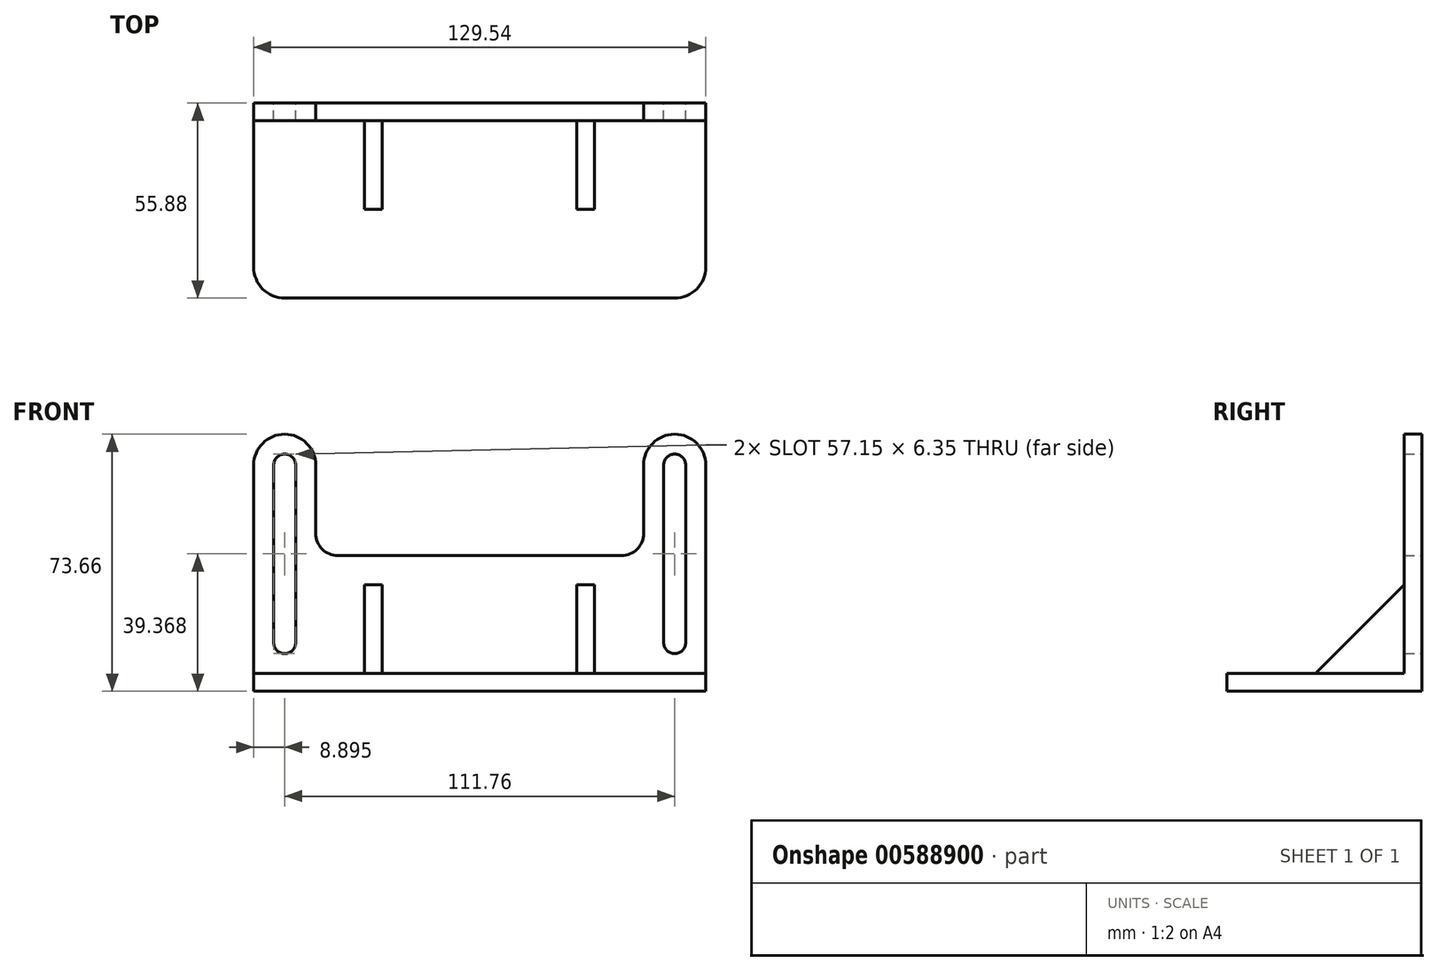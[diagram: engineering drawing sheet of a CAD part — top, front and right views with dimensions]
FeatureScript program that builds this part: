
annotation { "Feature Type Name" : "Feature", "Feature Type Description" : "" }
export const myFeature = defineFeature(function(context is Context, id is Id, definition is map)
    precondition{}
    {
        {
            var Q0;
            Q0=qCreatedBy(makeId("Front.planeOp"),FACE);
            var sketch = newSketch(context, id + "F0", { "sketchPlane" : qUnion([Q0])});
            skLineSegment(sketch, "E0.top", {"start": v(-62.17, -38.86) * mm, "end": v(67.37, -38.86) * mm});
            skArc(sketch, "E1", {"start": v(-50.1, 25.9) * mm, "mid": v(-53.28, 29.08) * mm, "end": v(-56.45, 25.9) * mm});
            skArc(sketch, "E2", {"start": v(61.66, 25.9) * mm, "mid": v(58.48, 29.08) * mm, "end": v(55.3, 25.9) * mm});
            skArc(sketch, "E3", {"start": v(-56.45, -24.9) * mm, "mid": v(-53.28, -28.07) * mm, "end": v(-50.1, -24.9) * mm});
            skArc(sketch, "E4", {"start": v(55.3, -24.9) * mm, "mid": v(58.48, -28.07) * mm, "end": v(61.66, -24.9) * mm});
            skLineSegment(sketch, "E5", {"start": v(-62.17, 25.9) * mm, "end": v(-62.17, -38.86) * mm});
            skArc(sketch, "E6", {"start": v(-44.39, 25.9) * mm, "mid": v(-53.28, 34.8) * mm, "end": v(-62.17, 25.9) * mm});
            skLineSegment(sketch, "E7.MirrorCS", {"start": v(67.37, 25.9) * mm, "end": v(67.37, -38.86) * mm});
            skArc(sketch, "E8.MirrorCS", {"start": v(49.6, 25.9) * mm, "mid": v(58.48, 34.8) * mm, "end": v(67.37, 25.9) * mm});
            skLineSegment(sketch, "E9", {"start": v(-62.17, -33.78) * mm, "end": v(67.37, -33.78) * mm});
            skLineSegment(sketch, "E10", {"start": v(-56.45, 25.9) * mm, "end": v(-56.45, -24.9) * mm});
            skLineSegment(sketch, "E11", {"start": v(-50.1, 26.18) * mm, "end": v(-50.1, -24.9) * mm});
            skLineSegment(sketch, "E12", {"start": v(55.3, 26.12) * mm, "end": v(55.3, -24.9) * mm});
            skLineSegment(sketch, "E13", {"start": v(61.66, 25.9) * mm, "end": v(61.66, -24.9) * mm});
            skLineSegment(sketch, "E14", {"start": v(-38.04, 0) * mm, "end": v(43.24, 0) * mm});
            skLineSegment(sketch, "E15", {"start": v(49.6, 6.35) * mm, "end": v(49.6, 25.9) * mm});
            skLineSegment(sketch, "E16", {"start": v(-44.39, 25.9) * mm, "end": v(-44.39, 6.35) * mm});
            skPoint(sketch, "E17.visualSharp", {"position": v(-44.39, 0) * mm});
            skArc(sketch, "E17.filletArc", {"start": v(-44.39, 6.35) * mm, "mid": v(-42.53, 1.86) * mm, "end": v(-38.04, 0) * mm});
            skPoint(sketch, "E18.visualSharp", {"position": v(49.6, 0) * mm});
            skArc(sketch, "E18.filletArc", {"start": v(43.24, 0) * mm, "mid": v(47.73, 1.86) * mm, "end": v(49.6, 6.35) * mm});
            skSolve(sketch);
        }
        {
            var Q0;
            Q0=makeQuery(id+"F0.imprint","IMPRINT",FACE,{"disambiguationData":[TD([[makeQuery(id+"F0.imprint","IMPRINT",EDGE,{"derivedFrom":sQuery(id+"F0.wireOp",EDGE,"E1")}),-1.0]])]});
            extrude(context, id + "F1", {"entities" : qUnion([Q0]), "depth" : 5.08 * mm, "offsetDistance" : 25.4 * mm});
        }
        {
            var Q0;
            {var subQ0=sQuery(id+"F0.wireOp",EDGE,"E0.top");Q0=makeQuery(id+"F0.imprint","IMPRINT",FACE,{"disambiguationData":[TD([[makeQuery(id+"F0.imprint","IMPRINT",EDGE,{"derivedFrom":subQ0}),1.0]])]});}
            extrude(context, id + "F2", {"entities" : qUnion([Q0]), "operationType" : NewBodyOperationType.ADD, "depth" : 55.88 * mm, "offsetDistance" : 25.4 * mm});
        }
        {
            var Q0;
            Q0=makeQuery(id+"F2.opExtrude","SWEPT_FACE",FACE,{"disambiguationData":[OSD([sQuery(id+"F0.wireOp",EDGE,"E9")])]});
            var sketch = newSketch(context, id + "F3", { "sketchPlane" : qUnion([Q0])});
            skArc(sketch, "E19.0", {"start": v(-62.17, -47) * mm, "mid": v(-59.56, -53.28) * mm, "end": v(-53.28, -55.88) * mm});
            skArc(sketch, "E20.0", {"start": v(58.48, -55.88) * mm, "mid": v(64.77, -53.28) * mm, "end": v(67.37, -47) * mm});
            skLineSegment(sketch, "E21", {"start": v(-62.17, -47) * mm, "end": v(-62.17, -5.08) * mm});
            skLineSegment(sketch, "E22", {"start": v(-62.17, -5.08) * mm, "end": v(67.37, -5.08) * mm});
            skLineSegment(sketch, "E23", {"start": v(67.37, -5.08) * mm, "end": v(67.37, -47) * mm});
            skLineSegment(sketch, "E24", {"start": v(-53.28, -55.88) * mm, "end": v(58.48, -55.88) * mm});
            skSolve(sketch);
        }
        {
            var Q0;
            {var subQ0=sQuery(id+"F3.wireOp",EDGE,"YX0IWA5Z-HBLO-qUTV-YXh6-1eAOZRUiMZh8");Q0=makeQuery(id+"F3.imprint","IMPRINT",FACE,{"disambiguationData":[TD([[makeQuery(id+"F3.imprint","IMPRINT",EDGE,{"derivedFrom":subQ0}),1.0]])]});}
            var Q1;
            {var subQ0=sQuery(id+"F3.wireOp",EDGE,"E19.0");var subQ1=sQuery(id+"F0.wireOp",EDGE,"E9");var subQ4=makeQuery(id+"F2.opExtrude","CAP_EDGE",EDGE,{"disambiguationData":[OSD([subQ1])],"isStart":false});var subQ5=makeQuery(id+"F3.imprint","INTERSECT",VERTEX,{"derivedFrom":[subQ4,subQ0]});Q1=makeQuery(id+"F3.imprint","IMPRINT",FACE,{"disambiguationData":[TD([[makeQuery(id+"F3.imprint","IMPRINT",EDGE,{"disambiguationData":[TD([[subQ5,1.0]])],"derivedFrom":subQ4}),1.0]])]});}
            var Q2;
            {var subQ0=sQuery(id+"F3.wireOp",EDGE,"E20.0");var subQ1=sQuery(id+"F0.wireOp",EDGE,"E9");var subQ4=makeQuery(id+"F2.opExtrude","CAP_EDGE",EDGE,{"disambiguationData":[OSD([subQ1])],"isStart":false});var subQ5=makeQuery(id+"F3.imprint","INTERSECT",VERTEX,{"derivedFrom":[subQ4,subQ0]});Q2=makeQuery(id+"F3.imprint","IMPRINT",FACE,{"disambiguationData":[TD([[makeQuery(id+"F3.imprint","IMPRINT",EDGE,{"disambiguationData":[TD([[subQ5,-1.0]])],"derivedFrom":subQ4}),1.0]])]});}
            var Q3;
            Q3=makeQuery(id+"F3.imprint","IMPRINT",FACE,{"disambiguationData":[TD([[makeQuery(id+"F3.imprint","IMPRINT",EDGE,{"derivedFrom":sQuery(id+"F3.wireOp",EDGE,"PaWCYf2k-phhZ-NQoM-fGsm-SVJtMK4VAfwM")}),1.0]])]});
            var Q4;
            Q4=makeQuery(id+"F3.imprint","IMPRINT",FACE,{"disambiguationData":[TD([[makeQuery(id+"F3.imprint","IMPRINT",EDGE,{"derivedFrom":sQuery(id+"F3.wireOp",EDGE,"SzknWCxU-9gAI-bEzf-Qa0E-uHS1ZXFUclCi")}),1.0]])]});
            extrude(context, id + "F4", {"entities" : qUnion([Q0, Q1, Q2, Q3, Q4]), "operationType" : NewBodyOperationType.REMOVE, "oppositeDirection" : true, "depth" : 5.08 * mm, "offsetDistance" : 25.4 * mm});
        }
        {
            var Q0;
            Q0=qCreatedBy(makeId("Right.planeOp"),FACE);
            var sketch = newSketch(context, id + "F5", { "sketchPlane" : qUnion([Q0])});
            skLineSegment(sketch, "E25", {"start": v(-5.08, -8.38) * mm, "end": v(-5.08, -33.78) * mm});
            skLineSegment(sketch, "E26.MirrorCS", {"start": v(-5.08, -33.78) * mm, "end": v(-30.48, -33.78) * mm});
            skLineSegment(sketch, "E27", {"start": v(-5.08, -8.38) * mm, "end": v(-30.48, -33.78) * mm});
            skSolve(sketch);
        }
        {
            var Q0;
            Q0=makeQuery(id+"F5.imprint","IMPRINT",FACE,{"disambiguationData":[TD([[makeQuery(id+"F5.imprint","IMPRINT",EDGE,{"derivedFrom":sQuery(id+"F5.wireOp",EDGE,"mLzi9KMf-18WF-i6Ga-XWjA-hkMFzDN3mARC")}),1.0]])]});
            var Q1;
            Q1=makeQuery(id+"F5.imprint","IMPRINT",FACE,{"disambiguationData":[TD([[makeQuery(id+"F5.imprint","IMPRINT",EDGE,{"derivedFrom":sQuery(id+"F5.wireOp",EDGE,"E25")}),-1.0]])]});
            extrude(context, id + "F6", {"entities" : qUnion([Q0, Q1]), "operationType" : NewBodyOperationType.ADD, "depth" : 35.56 * mm, "offsetDistance" : 25.4 * mm, "hasSecondDirection" : true, "secondDirectionOppositeDirection" : true, "secondDirectionDepth" : -30.48 * mm});
        }
        {
            var Q0;
            Q0=makeQuery(id+"F5.imprint","IMPRINT",FACE,{"disambiguationData":[TD([[makeQuery(id+"F5.imprint","IMPRINT",EDGE,{"derivedFrom":sQuery(id+"F5.wireOp",EDGE,"E25")}),-1.0]])]});
            extrude(context, id + "F7", {"entities" : qUnion([Q0]), "operationType" : NewBodyOperationType.ADD, "depth" : -30.48 * mm, "offsetDistance" : 25.4 * mm, "hasSecondDirection" : true, "secondDirectionOppositeDirection" : true, "secondDirectionDepth" : 25.4 * mm});
        }
    });
